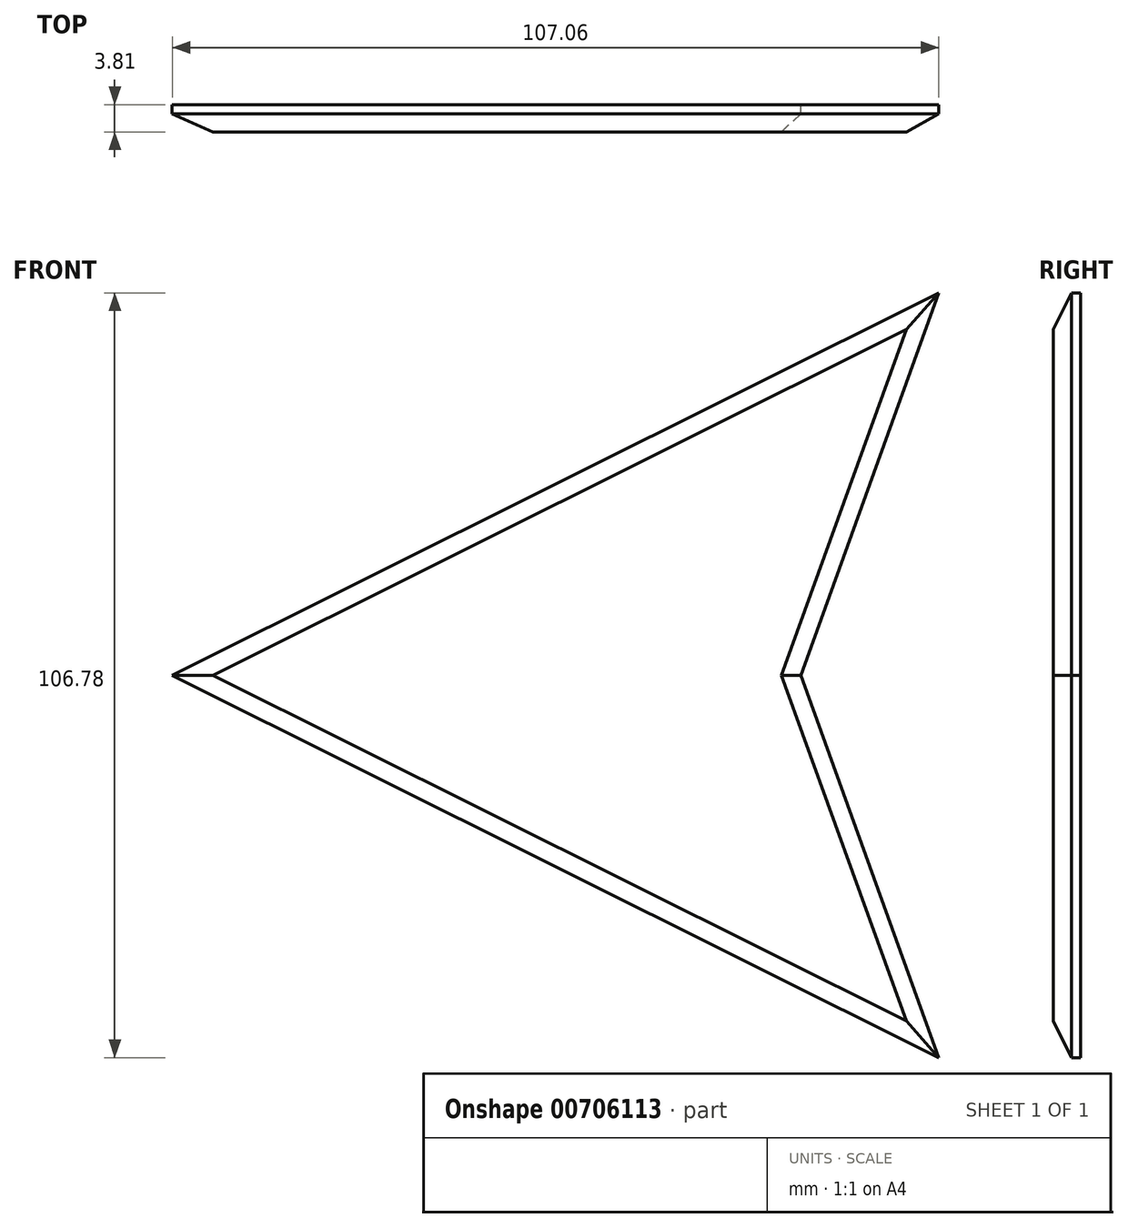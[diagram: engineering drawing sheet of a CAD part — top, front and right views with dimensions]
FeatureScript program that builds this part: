
annotation { "Feature Type Name" : "Feature", "Feature Type Description" : "" }
export const myFeature = defineFeature(function(context is Context, id is Id, definition is map)
    precondition{}
    {
        {
            var Q0;
            Q0=qCreatedBy(makeId("Front.planeOp"),FACE);
            var sketch = newSketch(context, id + "F0", { "sketchPlane" : qUnion([Q0])});
            skLineSegment(sketch, "E0", {"start": v(-59.14, 0) * mm, "end": v(47.92, 53.39) * mm});
            skLineSegment(sketch, "E1.MirrorCS", {"start": v(-59.14, 0) * mm, "end": v(47.92, -53.39) * mm});
            skLineSegment(sketch, "E2", {"start": v(47.92, 53.39) * mm, "end": v(28.64, 0) * mm});
            skLineSegment(sketch, "E3", {"start": v(47.92, -53.39) * mm, "end": v(28.64, 0) * mm});
            skSolve(sketch);
        }
        {
            var Q0;
            Q0=makeQuery(id+"F0.imprint","IMPRINT",FACE,{"disambiguationData":[TD([[makeQuery(id+"F0.imprint","IMPRINT",EDGE,{"derivedFrom":sQuery(id+"F0.wireOp",EDGE,"E0")}),-1.0]])]});
            extrude(context, id + "F1", {"entities" : qUnion([Q0]), "depth" : 3.8 * mm, "offsetDistance" : 25.4 * mm});
        }
        {
            var Q0;
            Q0=makeQuery(id+"F1.opExtrude","CAP_EDGE",EDGE,{"disambiguationData":[OSD([sQuery(id+"F0.wireOp",EDGE,"E0")])],"isStart":false});
            var Q1;
            Q1=makeQuery(id+"F1.opExtrude","CAP_EDGE",EDGE,{"disambiguationData":[OSD([sQuery(id+"F0.wireOp",EDGE,"E1.MirrorCS")])],"isStart":false});
            var Q2;
            Q2=makeQuery(id+"F1.opExtrude","CAP_EDGE",EDGE,{"disambiguationData":[OSD([sQuery(id+"F0.wireOp",EDGE,"E2")])],"isStart":false});
            var Q3;
            Q3=makeQuery(id+"F1.opExtrude","CAP_EDGE",EDGE,{"disambiguationData":[OSD([sQuery(id+"F0.wireOp",EDGE,"E3")])],"isStart":false});
            chamfer(context, id + "F2", {"entities" : qUnion([Q0, Q1, Q2, Q3]), "width" : 2.54 * mm, "tangentPropagation" : true});
        }
    });
